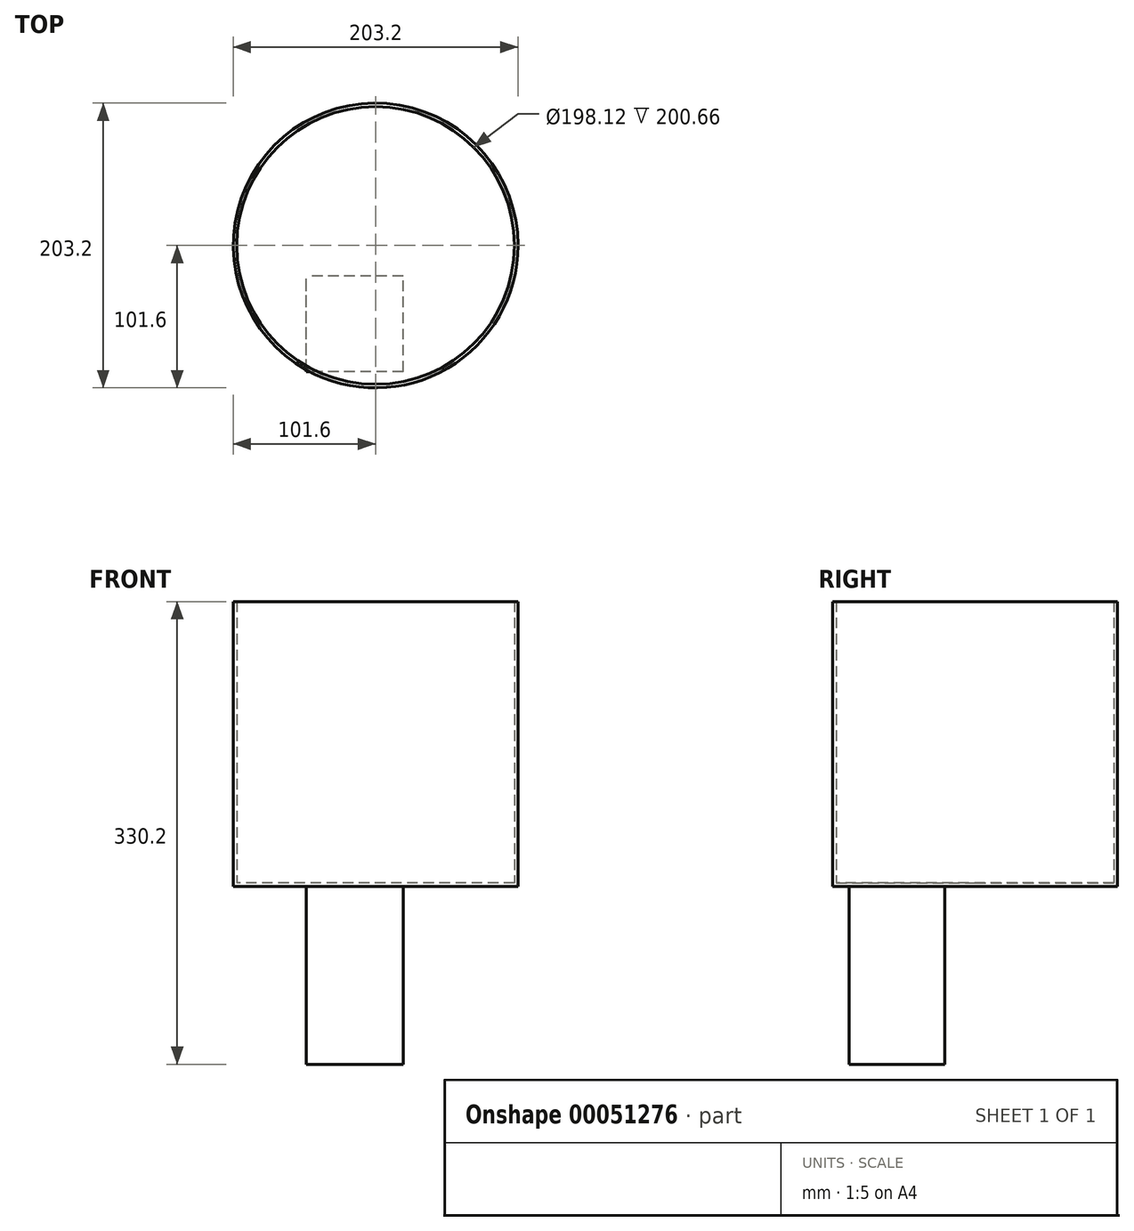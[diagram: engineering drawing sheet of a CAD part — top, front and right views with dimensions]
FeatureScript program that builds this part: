
annotation { "Feature Type Name" : "Feature", "Feature Type Description" : "" }
export const myFeature = defineFeature(function(context is Context, id is Id, definition is map)
    precondition{}
    {
        {
            var Q0;
            Q0=qCreatedBy(makeId("Top.planeOp"),FACE);
            var sketch = newSketch(context, id + "F0", { "sketchPlane" : qUnion([Q0])});
            skCircle(sketch, "E0", {"center": v(0, 0) * mm, "radius": 101.6 * mm});
            skSolve(sketch);
        }
        {
            var Q0;
            Q0 = qSketchRegion(id + "F0", true);
            extrude(context, id + "F1", {"entities" : qUnion([Q0]), "depth" : 203.2 * mm});
        }
        {
            var Q0;
            Q0=makeQuery(id+"F1.opExtrude","CAP_FACE",FACE,{"disambiguationData":[OSD([sQuery(id+"F0.wireOp",EDGE,"E0")])],"isStart":false});
            shell(context, id + "F2", {"entities" : qUnion([Q0]), "thickness" : 2.54 * mm});
        }
        {
            var Q0;
            Q0=makeQuery(id+"F1.opExtrude","CAP_FACE",FACE,{"disambiguationData":[OSD([sQuery(id+"F0.wireOp",EDGE,"E0")])],"isStart":true});
            var sketch = newSketch(context, id + "F3", { "sketchPlane" : qUnion([Q0])});
            skLineSegment(sketch, "E1.bottom", {"start": v(19.61, 89.97) * mm, "end": v(-49.36, 89.97) * mm});
            skLineSegment(sketch, "E1.top", {"start": v(19.61, 21.7) * mm, "end": v(-49.36, 21.7) * mm});
            skLineSegment(sketch, "E1.left", {"start": v(19.61, 89.97) * mm, "end": v(19.61, 21.7) * mm});
            skLineSegment(sketch, "E1.right", {"start": v(-49.36, 89.97) * mm, "end": v(-49.36, 21.7) * mm});
            skSolve(sketch);
        }
        {
            var Q0;
            {var subQ0=sQuery(id+"F3.wireOp",EDGE,"E1.right");var subQ1=sQuery(id+"F3.wireOp",EDGE,"E1.bottom");var subQ2=makeQuery(id+"F3.imprint","INTERSECT",VERTEX,{"derivedFrom":[subQ1,subQ0]});Q0=makeQuery(id+"F3.imprint","IMPRINT",FACE,{"disambiguationData":[TD([[makeQuery(id+"F3.imprint","IMPRINT",EDGE,{"disambiguationData":[TD([[subQ2,1.0]])],"derivedFrom":subQ1}),1.0]])]});}
            var Q1;
            {var subQ2=sQuery(id+"F3.wireOp",EDGE,"E1.top");Q1=makeQuery(id+"F3.imprint","IMPRINT",FACE,{"disambiguationData":[TD([[makeQuery(id+"F3.imprint","IMPRINT",EDGE,{"derivedFrom":subQ2}),-1.0]])]});}
            extrude(context, id + "F4", {"entities" : qUnion([Q0, Q1]), "operationType" : NewBodyOperationType.ADD, "depth" : 127 * mm});
        }
    });
